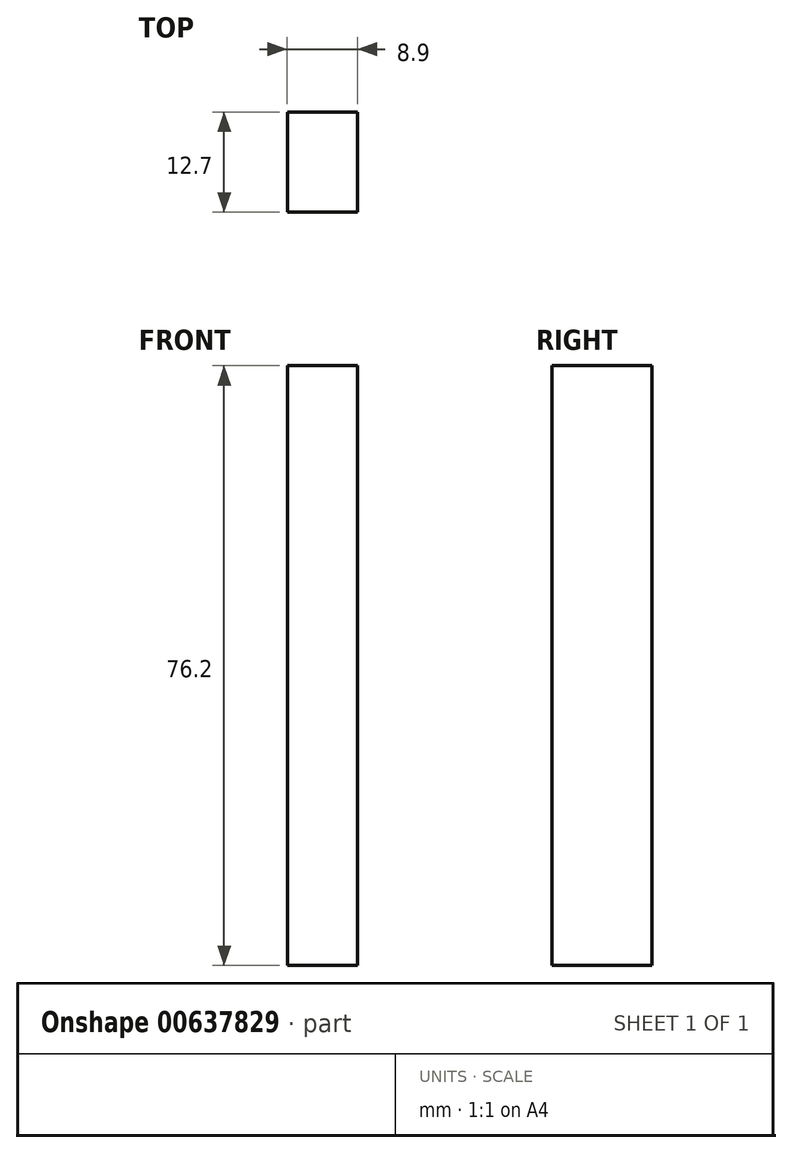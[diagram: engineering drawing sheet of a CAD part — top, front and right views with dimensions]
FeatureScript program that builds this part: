
annotation { "Feature Type Name" : "Feature", "Feature Type Description" : "" }
export const myFeature = defineFeature(function(context is Context, id is Id, definition is map)
    precondition{}
    {
        {
            var Q0;
            Q0=qCreatedBy(makeId("Front.planeOp"),FACE);
            var sketch = newSketch(context, id + "F0", { "sketchPlane" : qUnion([Q0])});
            skLineSegment(sketch, "E0.bottom", {"start": v(4.44, 38.1) * mm, "end": v(-4.45, 38.1) * mm});
            skLineSegment(sketch, "E0.top", {"start": v(4.44, -38.1) * mm, "end": v(-4.45, -38.1) * mm});
            skLineSegment(sketch, "E0.left", {"start": v(4.44, 38.1) * mm, "end": v(4.44, -38.1) * mm});
            skLineSegment(sketch, "E0.right", {"start": v(-4.45, 38.1) * mm, "end": v(-4.45, -38.1) * mm});
            skPoint(sketch, "E0.middle", {"position": v(0, 0) * mm});
            skSolve(sketch);
        }
        {
            var Q0;
            Q0 = qSketchRegion(id + "F0", true);
            extrude(context, id + "F1", {"entities" : qUnion([Q0]), "depth" : 12.7 * mm, "offsetDistance" : 25.4 * mm});
        }
    });
